# Revit family: COVETYP003
name_source: partatom
category: Furniture
units: mm (PartAtom-declared; Revit-internal decimal feet)

## family parameters
Always vertical = Yes
Cut with Voids When Loaded = No
OmniClass Number = 23.40.20.00
OmniClass Title = General Furniture and Specialties
Render Appearance Source = Family Geometry
Room Calculation Point = No
Shared = No
Work Plane-Based = No

## types (1)
- COVETYP003
    Cost = 13864 $
    Default Elevation = 0 mm  [stored 0 ft]
    Description = 2 x Chatham Cove 58H x 42W x 30D 2-Sided - Left - NonPowered, 2 x Chatham Cove 58H x 42W x 30D 2-Sided - Right - NonPowered, 4 x Chatham Cove - PET Tackboard for 58H x 30D, 1 x Tbl, Pbl, 2Mm, 30Dx72Wx16H, Stlt24, Gld
    Exported From CET Designer = Yes
    Manufacturer = AIS
    Model = F-CC2NL584230
    Show COVETYP003 = Yes
    VisibilityIndex = 0

note: [stored X ft] marks values corroborated as IEEE doubles in the binary element streams (Revit-internal decimal feet)

## geometry (parser evidence)
native form markers: Sweep x3
no freeform markers — native parametric forms only
